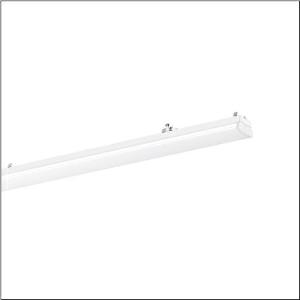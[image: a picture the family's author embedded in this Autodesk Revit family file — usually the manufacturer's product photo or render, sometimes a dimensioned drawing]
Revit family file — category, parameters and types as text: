
# Revit family: licross_r__21_recessed_opal_mo_52tl1ddn46xg_20ca
name_source: partatom
category: Lighting Fixtures
units: mm (PartAtom-declared; Revit-internal decimal feet)

## family parameters
Cut with Voids When Loaded = No
Host = Face
Light Source = No
Part Type = Normal
Room Calculation Point = No
Round Connector Dimension = Use Diameter
Shared = No

## types (1)
- --- (1 x LED, 6320 lm, 36.1 W, 4000K)
    Apparent Load = 36 VA
    CIE Flux Codes = 44 73 91 87 100
    Color Rendering = 80
    Color Temperature = 4000K
    Default Elevation = 1800 mm
    Description = Licross® 21 recessed opal MO, luminaire insert, of sheet steel, galvanised, coil coated, white, length: 1.500mm, width: 66mm, height: 67mm, LED rated luminous flux: 6.320lm, light colour: 840, control gear: DALI 2, with plug, 5-pole, with phase selection, mains connection: 220..240V, AC, 50/60Hz, rated input power: 36W, halogen-free wiring, primary optical cover: cover, of PMMA, light emission: direct with ceiling illumination distribution, primary light characteristic: symmetric, protection rating (complete): IP40, insulation class (complete): insulation class I (protective earthing), certification: CE, ENEC, VDE, UKCA, protection symbol: D if used in an environment without relevant dust loads with corresponding accessories, impact resistance: IK06, permissible ambient temperature for indoor applications: -25..+40°C, corresponds to IFS (International Featured Standards) requirements for safety and quality in the food industry, reducing of maximum allowable ambient temperature of 5°C with ceiling mounting, LABS conformity tested according to VDMA 24364:2018-05, packaging unit: 1 piece
    Height = 83 mm
    Lamp = 1 x LED
    Lamp Light Flux = 6320 lm
    Lamp Power = 36.1 W
    Lamp count = 1
    Length = 1500 mm
    Luminous efficacy = 175 lm/W
    Manufacturer = Siteco
    ModVariant = No
    Model = 52TL1DDN46XG
    Mounting Place = Ceiling
    Mounting Type = Pendant
    Number of Poles = 1
    OnlyDefault = Yes
    Power Factor = 1
    Product Name = Licross® 21 recessed opal MO
    Product group = luminaire insert
    ProductGroupID = 901
    Protection Class = Protection class I
    Protection Degree = IP 40
    RLX_Detail_Level = 1
    RLX_Emergency_Light_Flux = 0 lm
    RLX_Emergency_Type = 0
    RLX_Emergency_Type_DB = No
    RlxData = <blob elided: 26369 chars, md5=5fcdcb6e>
    Socket = socket
    Standby Power = 0 W
    System Light Flux = 6320 lm
    System Power = 36 W
    Type Comments = factory setting: luminous flux: 100 % | dim-lin: 254 | 245 mA
    Type Image = l_1313666.jpg
    URL = http://relux.com
    VarID = @adj_027093
    Voltage = 0 V
    Weight = 0.00 kg
    Width = 76 mm

## geometry (parser evidence)
native form markers: Blend x4, Sweep x11
no freeform markers — native parametric forms only
